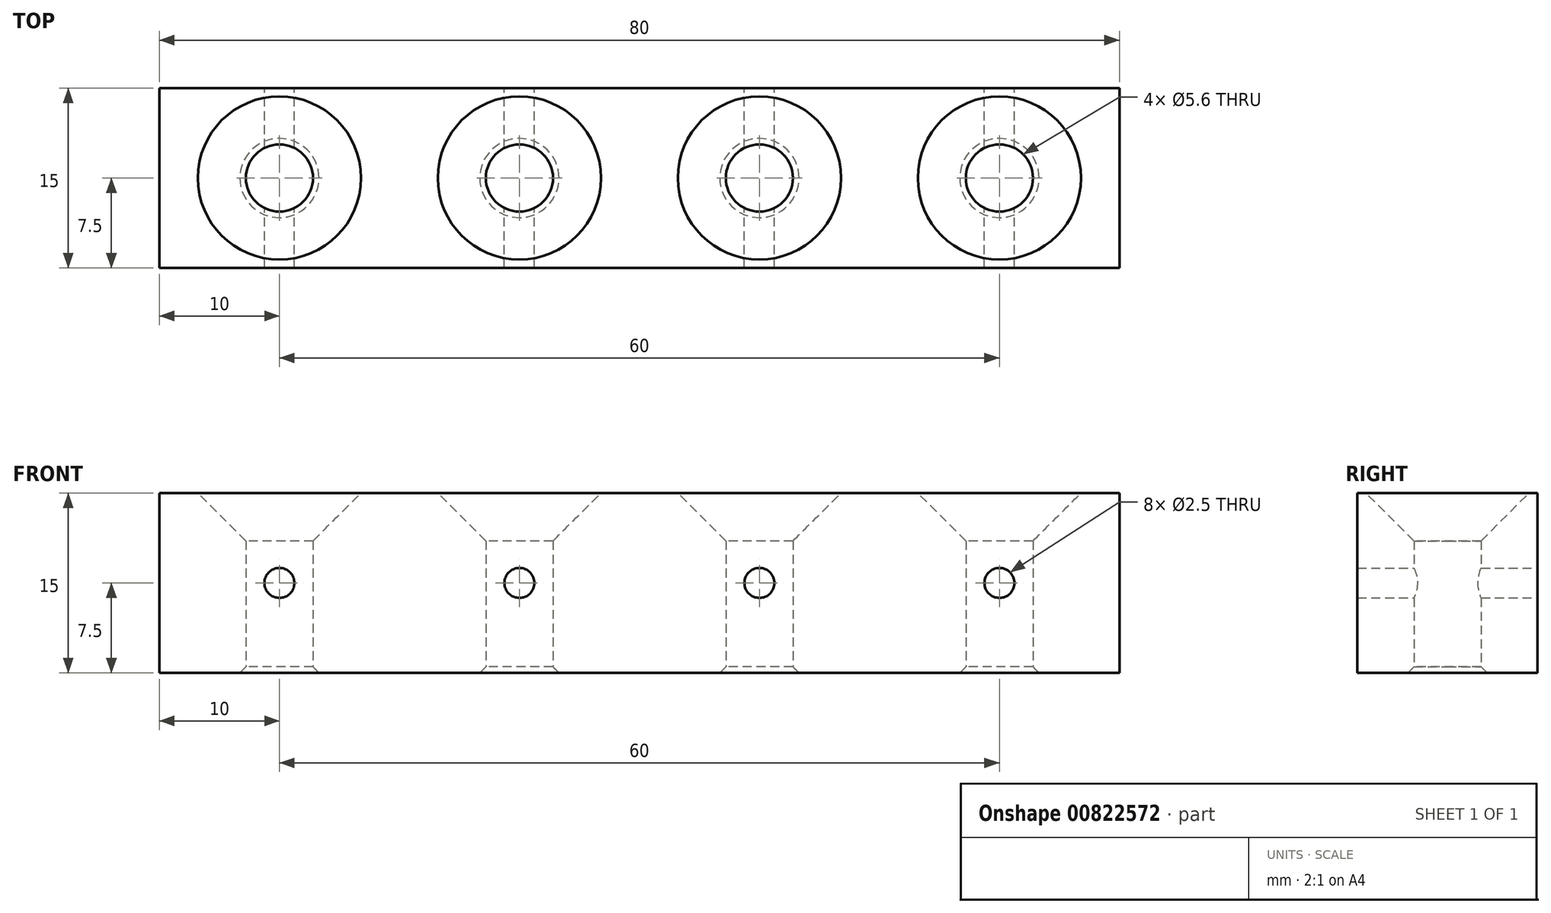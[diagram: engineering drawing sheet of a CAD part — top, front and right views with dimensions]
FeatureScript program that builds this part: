
annotation { "Feature Type Name" : "Feature", "Feature Type Description" : "" }
export const myFeature = defineFeature(function(context is Context, id is Id, definition is map)
    precondition{}
    {
        {
            var Q0;
            Q0=qCreatedBy(makeId("Top.planeOp"),FACE);
            var sketch = newSketch(context, id + "F0", { "sketchPlane" : qUnion([Q0])});
            skCircle(sketch, "E0", {"center": v(0, 0) * mm, "radius": 2.8 * mm});
            skCircle(sketch, "E1.1.0.0", {"center": v(20, 0) * mm, "radius": 2.8 * mm});
            skCircle(sketch, "E1.2.0.0", {"center": v(40, 0) * mm, "radius": 2.8 * mm});
            skCircle(sketch, "E1.3.0.0", {"center": v(60, 0) * mm, "radius": 2.8 * mm});
            skLineSegment(sketch, "E1.direction1", {"start": v(0, 0) * mm, "end": v(20, 0) * mm, "construction": true});
            skLineSegment(sketch, "E2.bottom", {"start": v(-10, 7.5) * mm, "end": v(70, 7.5) * mm});
            skLineSegment(sketch, "E2.top", {"start": v(-10, -7.5) * mm, "end": v(70, -7.5) * mm});
            skLineSegment(sketch, "E2.left", {"start": v(-10, 7.5) * mm, "end": v(-10, -7.5) * mm});
            skLineSegment(sketch, "E2.right", {"start": v(70, 7.5) * mm, "end": v(70, -7.5) * mm});
            skPoint(sketch, "E3", {"position": v(70, 0) * mm});
            skSolve(sketch);
        }
        {
            var Q0;
            Q0=makeQuery(id+"F0.imprint","IMPRINT",FACE,{"disambiguationData":[TD([[makeQuery(id+"F0.imprint","IMPRINT",EDGE,{"derivedFrom":sQuery(id+"F0.wireOp",EDGE,"E0")}),-1.0]])]});
            extrude(context, id + "F1", {"entities" : qUnion([Q0]), "endBound" : BoundingType.SYMMETRIC, "depth" : 15 * mm, "offsetDistance" : 25 * mm});
        }
        {
            var Q0;
            Q0=makeQuery(id+"F1.opExtrude","CAP_EDGE",EDGE,{"disambiguationData":[OSD([sQuery(id+"F0.wireOp",EDGE,"E0")])],"isStart":false});
            var Q1;
            Q1=makeQuery(id+"F1.opExtrude","CAP_EDGE",EDGE,{"disambiguationData":[OSD([sQuery(id+"F0.wireOp",EDGE,"E1.1.0.0")])],"isStart":false});
            var Q2;
            Q2=makeQuery(id+"F1.opExtrude","CAP_EDGE",EDGE,{"disambiguationData":[OSD([sQuery(id+"F0.wireOp",EDGE,"E1.2.0.0")])],"isStart":false});
            var Q3;
            Q3=makeQuery(id+"F1.opExtrude","CAP_EDGE",EDGE,{"disambiguationData":[OSD([sQuery(id+"F0.wireOp",EDGE,"E1.3.0.0")])],"isStart":false});
            chamfer(context, id + "F2", {"entities" : qUnion([Q0, Q1, Q2, Q3]), "width" : 4 * mm, "tangentPropagation" : true});
        }
        {
            var Q0;
            Q0=makeQuery(id+"F1.opExtrude","CAP_EDGE",EDGE,{"disambiguationData":[OSD([sQuery(id+"F0.wireOp",EDGE,"E1.3.0.0")])],"isStart":true});
            var Q1;
            Q1=makeQuery(id+"F1.opExtrude","CAP_EDGE",EDGE,{"disambiguationData":[OSD([sQuery(id+"F0.wireOp",EDGE,"E1.2.0.0")])],"isStart":true});
            var Q2;
            Q2=makeQuery(id+"F1.opExtrude","CAP_EDGE",EDGE,{"disambiguationData":[OSD([sQuery(id+"F0.wireOp",EDGE,"E1.1.0.0")])],"isStart":true});
            var Q3;
            Q3=makeQuery(id+"F1.opExtrude","CAP_EDGE",EDGE,{"disambiguationData":[OSD([sQuery(id+"F0.wireOp",EDGE,"E0")])],"isStart":true});
            chamfer(context, id + "F3", {"entities" : qUnion([Q0, Q1, Q2, Q3]), "width" : 0.5 * mm, "tangentPropagation" : true});
        }
        {
            var Q0;
            Q0=makeQuery(id+"F1.opExtrude","SWEPT_FACE",FACE,{"disambiguationData":[OSD([sQuery(id+"F0.wireOp",EDGE,"E2.bottom")])]});
            var sketch = newSketch(context, id + "F4", { "sketchPlane" : qUnion([Q0])});
            skPoint(sketch, "E4", {"position": v(-60, 0) * mm});
            skPoint(sketch, "E5", {"position": v(-40, 0) * mm});
            skPoint(sketch, "E6", {"position": v(-20, 0) * mm});
            skPoint(sketch, "E7", {"position": v(0, 0) * mm});
            skSolve(sketch);
        }
        {
            var Q0;
            Q0=sQuery(id+"F4.wireOp",VERTEX,"E4");
            var Q1;
            Q1=sQuery(id+"F4.wireOp",VERTEX,"E5");
            var Q2;
            Q2=sQuery(id+"F4.wireOp",VERTEX,"E6");
            var Q3;
            Q3=sQuery(id+"F4.wireOp",VERTEX,"E7");
            var Q4;
            Q4=makeQuery(id+"F1.opExtrude","SWEPT_BODY",BODY,{"disambiguationData":[OSD([sQuery(id+"F0.wireOp",EDGE,"E0"),sQuery(id+"F0.wireOp",EDGE,"E1.1.0.0"),sQuery(id+"F0.wireOp",EDGE,"E1.2.0.0"),sQuery(id+"F0.wireOp",EDGE,"E1.3.0.0"),sQuery(id+"F0.wireOp",EDGE,"E2.bottom"),sQuery(id+"F0.wireOp",EDGE,"E2.top"),sQuery(id+"F0.wireOp",EDGE,"E2.left"),sQuery(id+"F0.wireOp",EDGE,"E2.right")])]});
            hole(context, id + "F5", {"style" : HoleStyle.SIMPLE, "endStyle" : HoleEndStyle.THROUGH, "holeDiameter" : 2.5 * mm, "majorDiameter" : 5 * mm, "isTappedThrough" : true, "tappedDepth" : 12 * mm, "tapClearance" : 3, "locations" : qUnion([Q0, Q1, Q2, Q3]), "scope" : qUnion([Q4])});
        }
    });
